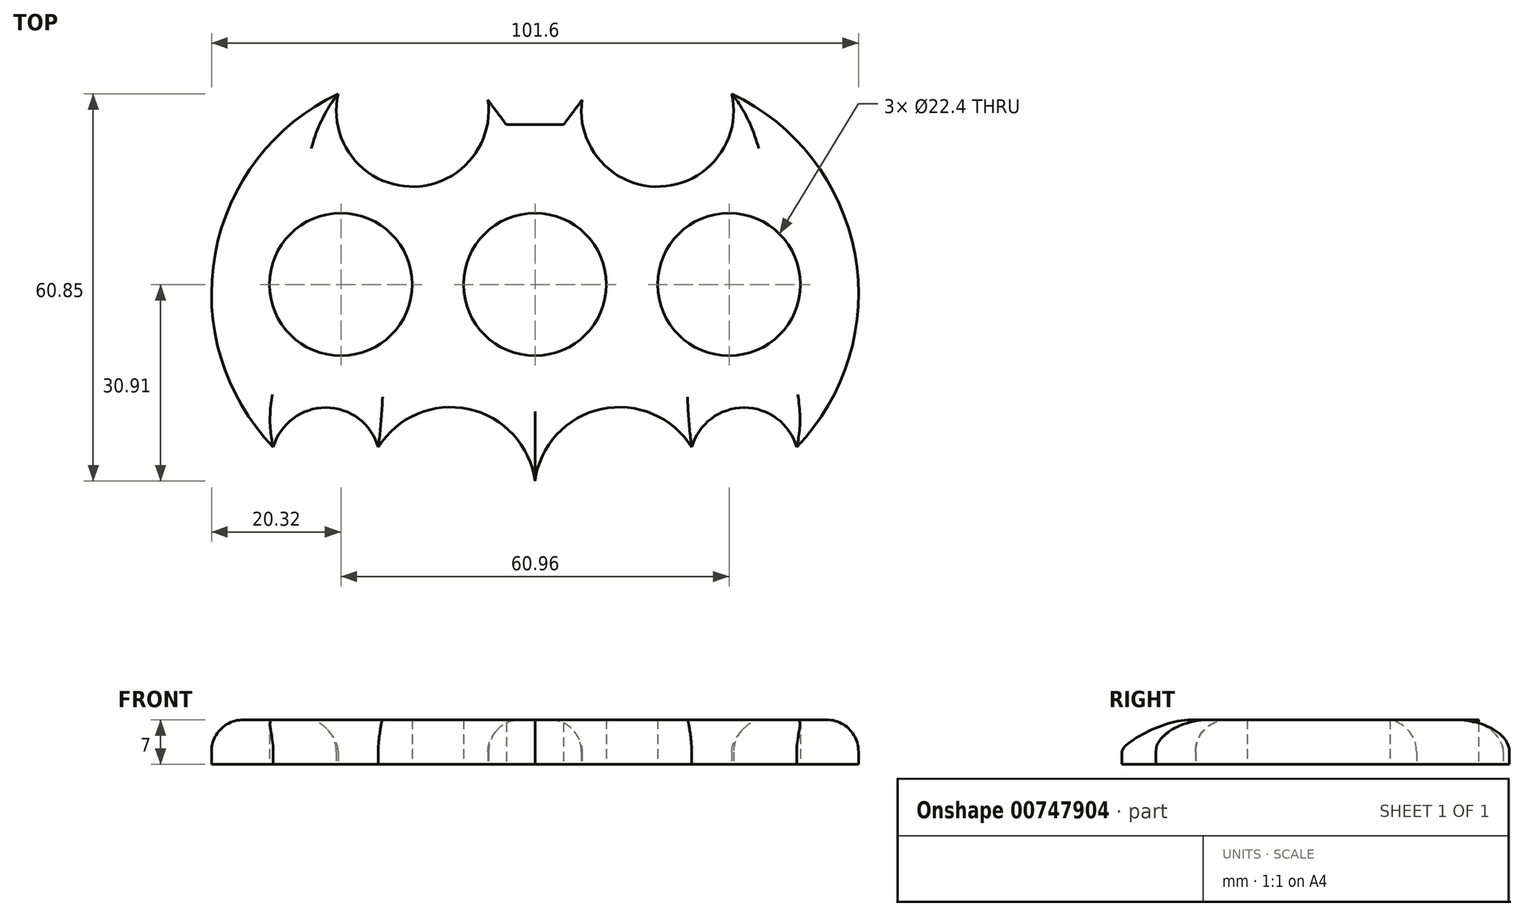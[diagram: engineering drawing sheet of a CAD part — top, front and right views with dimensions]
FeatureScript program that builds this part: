
annotation { "Feature Type Name" : "Feature", "Feature Type Description" : "" }
export const myFeature = defineFeature(function(context is Context, id is Id, definition is map)
    precondition{}
    {
        {
            var Q0;
            Q0=qCreatedBy(makeId("Top.planeOp"),FACE);
            var sketch = newSketch(context, id + "F0", { "sketchPlane" : qUnion([Q0])});
            skCircle(sketch, "E0", {"center": v(0, 0) * mm, "radius": 11.2 * mm});
            skLineSegment(sketch, "E1", {"start": v(0, 0) * mm, "end": v(30.48, 0) * mm});
            skCircle(sketch, "E2", {"center": v(30.48, 0) * mm, "radius": 11.2 * mm});
            skCircle(sketch, "E3.MirrorC", {"center": v(-30.48, 0) * mm, "radius": 11.2 * mm});
            skArc(sketch, "E4", {"start": v(-30.91, 29.94) * mm, "mid": v(-50.23, 4.8) * mm, "end": v(-41.1, -25.58) * mm});
            skArc(sketch, "E5", {"start": v(-24.6, -25.58) * mm, "mid": v(-32.85, -19.36) * mm, "end": v(-41.1, -25.58) * mm});
            skArc(sketch, "E6", {"start": v(0, -30.91) * mm, "mid": v(-10.43, -19.6) * mm, "end": v(-24.6, -25.58) * mm});
            skArc(sketch, "E7", {"start": v(-30.91, 29.94) * mm, "mid": v(-19.73, 15.37) * mm, "end": v(-7.4, 28.97) * mm});
            skLineSegment(sketch, "E8", {"start": v(-7.4, 28.97) * mm, "end": v(-4.49, 25.1) * mm});
            skLineSegment(sketch, "E9", {"start": v(-4.49, 25.1) * mm, "end": v(0, 25.1) * mm});
            skLineSegment(sketch, "E10.MirrorCS", {"start": v(4.49, 25.1) * mm, "end": v(0, 25.1) * mm});
            skLineSegment(sketch, "E11.MirrorCS", {"start": v(7.4, 28.97) * mm, "end": v(4.49, 25.1) * mm});
            skArc(sketch, "E12.MirrorCS", {"start": v(30.91, 29.94) * mm, "mid": v(19.73, 15.37) * mm, "end": v(7.4, 28.97) * mm});
            skArc(sketch, "E13.MirrorCS", {"start": v(30.91, 29.94) * mm, "mid": v(50.23, 4.8) * mm, "end": v(41.1, -25.58) * mm});
            skArc(sketch, "E14.MirrorCS", {"start": v(24.6, -25.58) * mm, "mid": v(32.85, -19.36) * mm, "end": v(41.1, -25.58) * mm});
            skArc(sketch, "E15.MirrorCS", {"start": v(0, -30.91) * mm, "mid": v(10.43, -19.6) * mm, "end": v(24.6, -25.58) * mm});
            skSolve(sketch);
        }
        {
            var Q0;
            Q0=makeQuery(id+"F0.imprint","IMPRINT",FACE,{"disambiguationData":[TD([[makeQuery(id+"F0.imprint","IMPRINT",EDGE,{"derivedFrom":sQuery(id+"F0.wireOp",EDGE,"E0")}),-1.0]])]});
            extrude(context, id + "F1", {"entities" : qUnion([Q0]), "depth" : 7 * mm, "offsetDistance" : 25 * mm});
        }
        {
            var Q0;
            Q0=makeQuery(id+"F1.opExtrude","CAP_EDGE",EDGE,{"disambiguationData":[OSD([sQuery(id+"F0.wireOp",EDGE,"E4")])],"isStart":false});
            var Q1;
            Q1=makeQuery(id+"F1.opExtrude","CAP_EDGE",EDGE,{"disambiguationData":[OSD([sQuery(id+"F0.wireOp",EDGE,"E7")])],"isStart":false});
            var Q2;
            Q2=makeQuery(id+"F1.opExtrude","CAP_EDGE",EDGE,{"disambiguationData":[OSD([sQuery(id+"F0.wireOp",EDGE,"E12.MirrorCS")])],"isStart":false});
            var Q3;
            Q3=makeQuery(id+"F1.opExtrude","CAP_EDGE",EDGE,{"disambiguationData":[OSD([sQuery(id+"F0.wireOp",EDGE,"E13.MirrorCS")])],"isStart":false});
            var Q4;
            Q4=makeQuery(id+"F1.opExtrude","CAP_EDGE",EDGE,{"disambiguationData":[OSD([sQuery(id+"F0.wireOp",EDGE,"E14.MirrorCS")])],"isStart":false});
            var Q5;
            Q5=makeQuery(id+"F1.opExtrude","CAP_EDGE",EDGE,{"disambiguationData":[OSD([sQuery(id+"F0.wireOp",EDGE,"E15.MirrorCS")])],"isStart":false});
            var Q6;
            Q6=makeQuery(id+"F1.opExtrude","CAP_EDGE",EDGE,{"disambiguationData":[OSD([sQuery(id+"F0.wireOp",EDGE,"E6")])],"isStart":false});
            var Q7;
            Q7=makeQuery(id+"F1.opExtrude","CAP_EDGE",EDGE,{"disambiguationData":[OSD([sQuery(id+"F0.wireOp",EDGE,"E5")])],"isStart":false});
            fillet(context, id + "F2", {"entities" : qUnion([Q0, Q1, Q2, Q3, Q4, Q5, Q6, Q7]), "radius" : 5 * mm, "tangentPropagation" : true, "allowEdgeOverflow" : false});
        }
    });
